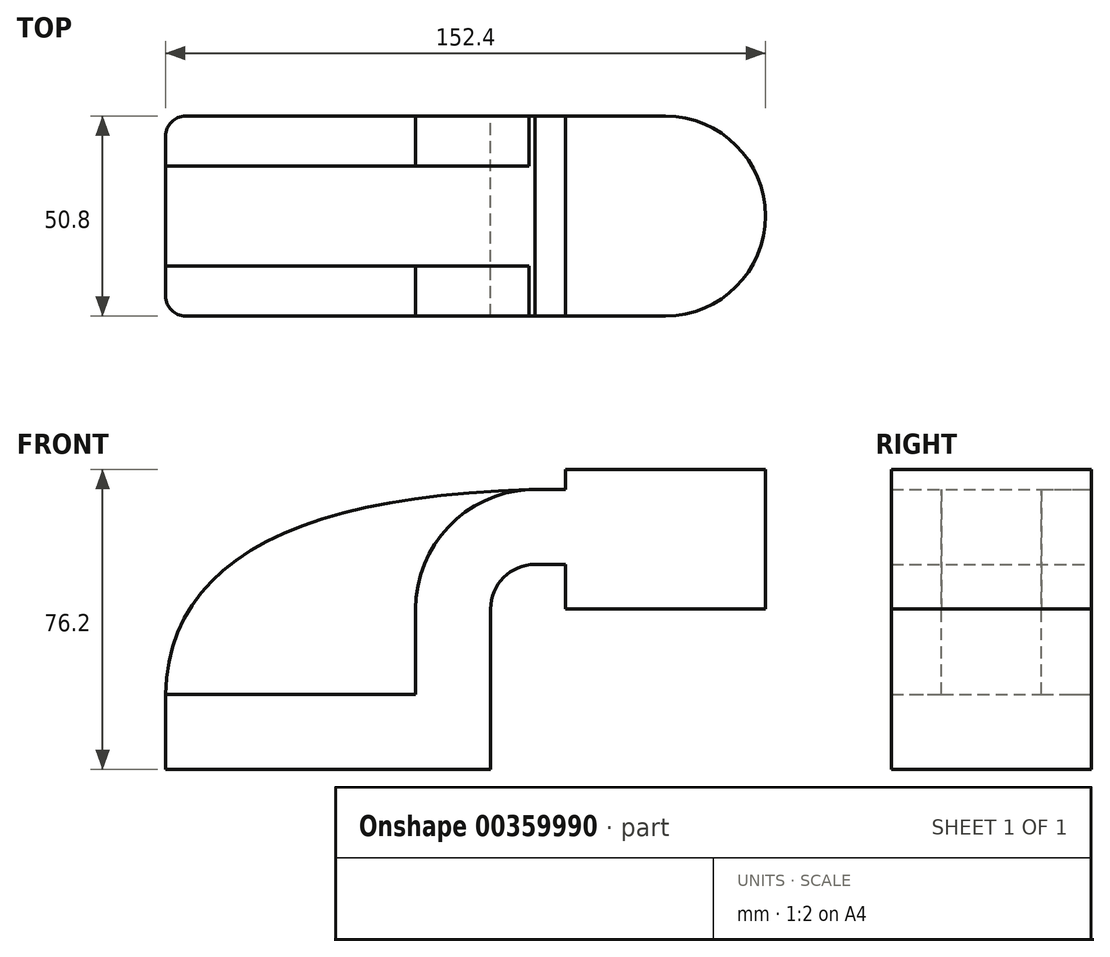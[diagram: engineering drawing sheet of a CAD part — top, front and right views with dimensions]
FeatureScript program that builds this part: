
annotation { "Feature Type Name" : "Feature", "Feature Type Description" : "" }
export const myFeature = defineFeature(function(context is Context, id is Id, definition is map)
    precondition{}
    {
        {
            var Q0;
            Q0=qCreatedBy(makeId("Front.planeOp"),FACE);
            var sketch = newSketch(context, id + "F0", { "sketchPlane" : qUnion([Q0])});
            skLineSegment(sketch, "E0.bottom", {"start": v(41.28, -9.52) * mm, "end": v(-41.27, -9.53) * mm});
            skLineSegment(sketch, "E0.top", {"start": v(41.27, 9.53) * mm, "end": v(-41.28, 9.53) * mm});
            skLineSegment(sketch, "E0.left", {"start": v(41.28, -9.52) * mm, "end": v(41.28, 9.53) * mm});
            skLineSegment(sketch, "E0.right", {"start": v(-41.27, -9.53) * mm, "end": v(-41.28, 9.53) * mm});
            skPoint(sketch, "E0.middle", {"position": v(0, 0) * mm});
            skLineSegment(sketch, "E1.bottom", {"start": v(60.33, 66.68) * mm, "end": v(111.13, 66.68) * mm});
            skLineSegment(sketch, "E1.top", {"start": v(60.32, 31.19) * mm, "end": v(111.13, 31.19) * mm});
            skLineSegment(sketch, "E1.left", {"start": v(60.33, 66.68) * mm, "end": v(60.33, 31.19) * mm});
            skLineSegment(sketch, "E1.right", {"start": v(111.13, 66.68) * mm, "end": v(111.12, 31.19) * mm});
            skPoint(sketch, "E1.middle", {"position": v(85.73, 48.93) * mm});
            skLineSegment(sketch, "E2", {"start": v(41.27, 9.53) * mm, "end": v(41.27, 31.19) * mm});
            skArc(sketch, "E3", {"start": v(41.27, 31.19) * mm, "mid": v(44.6, 39.22) * mm, "end": v(52.63, 42.55) * mm});
            skLineSegment(sketch, "E4", {"start": v(52.63, 42.55) * mm, "end": v(85.39, 42.55) * mm});
            skLineSegment(sketch, "E5.0", {"start": v(52.63, 61.6) * mm, "end": v(85.39, 61.6) * mm});
            skArc(sketch, "E5.1", {"start": v(22.22, 31.19) * mm, "mid": v(31.13, 52.69) * mm, "end": v(52.63, 61.6) * mm});
            skLineSegment(sketch, "E5.2", {"start": v(22.22, 9.53) * mm, "end": v(22.22, 31.19) * mm});
            skLineSegment(sketch, "E6", {"start": v(85.72, 31.19) * mm, "end": v(85.72, 66.68) * mm});
            skFitSpline(sketch, "E7", {"points": [v(-41.28, 9.53) * mm, v(52.63, 61.6) * mm], "startDerivative": vector(2.03, 99.63) * mm, "endDerivative": vector(185.78, 4.51) * mm});
            skSolve(sketch);
        }
        {
            var Q0;
            Q0=makeQuery(id+"F0.imprint","IMPRINT",FACE,{"disambiguationData":[TD([[makeQuery(id+"F0.imprint","IMPRINT",EDGE,{"derivedFrom":sQuery(id+"F0.wireOp",EDGE,"E0.bottom")}),-1.0]])]});
            extrude(context, id + "F1", {"entities" : qUnion([Q0]), "endBound" : BoundingType.SYMMETRIC, "depth" : 50.8 * mm});
        }
        {
            var Q0;
            {var subQ1=sQuery(id+"F0.wireOp",EDGE,"E2");Q0=makeQuery(id+"F0.imprint","IMPRINT",FACE,{"disambiguationData":[TD([[makeQuery(id+"F0.imprint","IMPRINT",EDGE,{"derivedFrom":subQ1}),1.0]])]});}
            var Q1;
            {var subQ4=sQuery(id+"F0.wireOp",EDGE,"E6");Q1=makeQuery(id+"F0.imprint","IMPRINT",FACE,{"disambiguationData":[TD([[makeQuery(id+"F0.imprint","IMPRINT",EDGE,{"derivedFrom":subQ4}),1.0]])]});}
            extrude(context, id + "F2", {"entities" : qUnion([Q0, Q1]), "operationType" : NewBodyOperationType.ADD, "endBound" : BoundingType.SYMMETRIC, "depth" : 50.8 * mm});
        }
        {
            var Q0;
            {var subQ3=sQuery(id+"F0.wireOp",EDGE,"E5.2");Q0=makeQuery(id+"F0.imprint","IMPRINT",FACE,{"disambiguationData":[TD([[makeQuery(id+"F0.imprint","IMPRINT",EDGE,{"derivedFrom":subQ3}),1.0]])]});}
            extrude(context, id + "F3", {"entities" : qUnion([Q0]), "operationType" : NewBodyOperationType.ADD, "endBound" : BoundingType.SYMMETRIC, "depth" : 25.4 * mm});
        }
        {
            var Q0;
            {var subQ0=sQuery(id+"F0.wireOp",EDGE,"E1.right");Q0=makeQuery(id+"F0.imprint","IMPRINT",FACE,{"disambiguationData":[TD([[makeQuery(id+"F0.imprint","IMPRINT",EDGE,{"derivedFrom":subQ0}),-1.0]])]});}
            var Q1;
            Q1=sQuery(id+"F0.wireOp",EDGE,"E6");
            revolve(context, id + "F4", {"operationType" : NewBodyOperationType.ADD, "entities" : qUnion([Q0]), "axis" : qUnion([Q1]), "revolveType" : RevolveType.FULL});
        }
        {
            var Q0;
            Q0=makeQuery(id+"F1.opExtrude","CAP_EDGE",EDGE,{"disambiguationData":[OSD([sQuery(id+"F0.wireOp",EDGE,"E0.right")])],"isStart":false});
            var Q1;
            Q1=makeQuery(id+"F1.opExtrude","CAP_EDGE",EDGE,{"disambiguationData":[OSD([sQuery(id+"F0.wireOp",EDGE,"E0.right")])],"isStart":true});
            fillet(context, id + "F5", {"entities" : qUnion([Q0, Q1]), "radius" : 5.08 * mm, "tangentPropagation" : true, "allowEdgeOverflow" : false});
        }
    });
